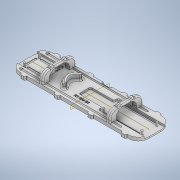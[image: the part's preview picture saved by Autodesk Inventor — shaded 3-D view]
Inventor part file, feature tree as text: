
AUTODESK INVENTOR PART (.ipt)
format: ipt  version: 2021 (Build 250183000, 183)  size: 3,149,312 bytes
history: native  units: in
note: dims shown in document units (in); Inventor stores cm internally (conversion verified against a paired STEP export)
features: fillet x15, extrude x14, sketch x14, mirror x8, plane x2, chamfer x2, revolve x1
ambient origin geometry x8: Origin, YZ Plane, XZ Plane, XY Plane, X Axis, Y Axis, Z Axis, Center Point
bodies: Solid1 (feature_tree)
feature tree (56):
  extrude  "Extrusion1"  Depth=4.9606in
  extrude  "Extrusion2"  TaperAngle=0.0deg  [1 undecoded]
  plane  "Work Plane1"
  plane  "Work Plane2"
  extrude  "Extrusion5"  Depth=0.2362in
  fillet  "Fillet2"  Radius=0.0787in
  mirror  "Mirror3"
  extrude  "Extrusion6"  TaperAngle=0.0deg  [1 undecoded]
  extrude  "Extrusion7"  Depth=0.2362in
  extrude  "Extrusion9"  [1 undecoded]
  extrude  "Extrusion10"  Depth=0.5354in
  fillet  "Fillet4"  Radius=0.9449in
  mirror  "Mirror4"
  mirror  "Mirror5"
  fillet  "Fillet5"  Radius=2.7559in
  extrude  "Extrusion11"  Depth=0.811in
  fillet  "Fillet6"  Radius=0.0866in
  extrude  "Extrusion12"  Depth=0.0945in
  extrude  "Extrusion13"  Depth=0.0945in
  mirror  "Mirror8"
  mirror  "Mirror9"
  mirror  "Mirror10"
  fillet  "Fillet9"  [1 undecoded]
  fillet  "Fillet11"  [1 undecoded]
  fillet  "Fillet12"  [1 undecoded]
  extrude  "Extrusion17"  Depth=0.7in
  fillet  "Fillet16"  Radius=1.8in
  mirror  "Mirror13"
  extrude  "Extrusion20"  Depth=0.1575in TaperAngle=0.0deg
  fillet  "Fillet20"  Radius=1.9685in
  revolve  "Revolution8"  [1 undecoded]
  mirror  "Mirror15"
  extrude  "Extrusion22"  Depth=0.0945in
  extrude  "Extrusion23"  Depth=0.0945in
  chamfer  "Chamfer4"  Distance=0.0945in
  fillet  "Fillet24"  Radius=0.0945in
  fillet  "Fillet25"  [1 undecoded]
  chamfer  "Chamfer5"  [1 undecoded]
  fillet  "Fillet28"  [1 undecoded]
  fillet  "Fillet29"  [1 undecoded]
  fillet  "Fillet30"  Radius=0.9in
  fillet  "Fillet31"  Radius=0.7in
  sketch  "Sketch1"  dims[d0=0.1575in d1=0.0in d2=4.9606in]
  sketch  "Sketch2"  dims[d3=1.5512in d4=0.0in]
  sketch  "Sketch7"  dims[d5=0.0in d6=0.2362in d7=0.0787in d8=0.0in]
  sketch  "Sketch8"  dims[d15=-0.7756in d16=0.0in]
  sketch  "Sketch13"  dims[d17=0.0in d18=0.2362in]
  sketch  "Sketch14"  dims[d19=1.3386in d24=-2.4803in]
  sketch  "Sketch15"  dims[d28=0.5354in d29=0.0in d30=0.5354in d31=0.9449in d32=2.7559in]
  sketch  "Sketch25"  dims[d33=0.4724in d34=0.811in d35=0.0866in d36=0.0in]
  sketch  "Sketch27"  dims[d37=0.0945in d38=0.0945in]
  sketch  "Sketch39"  dims[d39=0.0945in d40=0.0945in d41=0.0in d42=0.0in d43=0.0in]
  sketch  "Sketch44"  dims[d44=0.0in d45=0.7in d46=1.8in]
  sketch  "Sketch47"  dims[d47=0.35in d48=0.1575in d49=0.0in d60=1.9685in]
  sketch  "Sketch49"  dims[d61=0.9449in d62=0.4724in]
  sketch  "Sketch50"  dims[d63=1.7087in d64=0.0945in d65=0.0945in d66=0.0945in d67=0.0945in d68=0.0in d69=0.0in d70=0.0in d71=0.0in d72=0.9in d73=0.7in d74=0.35in d75=0.1969in d79=0.4094in d80=0.0in d81=0.0in d82=0.0in d83=0.0in d84=0.0in d85=0.0787in d86=0.0in d88=0.3543in d89=0.315in d90=0.2362in d92=0.0394in d93=0.0in d96=1.1024in d97=0.5512in d98=0.2756in d99=0.0787in d116=0.2362in d117=0.0in d118=0.0in d119=0.1181in d120=0.0394in d121=0.0in d126=0.0787in d127=0.0157in d128=0.0in d131=0.0394in d133=0.0551in d134=0.0in d138=0.5709in d147=0.2362in d148=0.0591in d171=0.0866in d172=0.0394in d173=0.0394in d174=0.0866in d175=0.2638in d176=0.0866in d177=0.0945in d178=0.0866in d179=0.0394in d180=0.0394in d181=0.0787in d182=0.0236in d183=0.0in d184=0.0433in d204=0.0945in d211=0.3937in d212=0.0in d213=0.0787in d214=4.4094in d215=0.0in d216=0.0394in d228=180.0deg d229=0.0394in d230=0.0197in d232=0.0in d233=0.0394in d240=0.0in d243=0.0in d244=0.0in d245=0.0in d246=0.1575in d247=0.1575in d248=0.315in d249=0.315in d250=0.0in d253=0.3937in d254=0.0787in d255=0.1969in d256=0.0787in d257=0.0in d258=0.0787in d259=0.0394in d260=45.0deg d261=0.0787in d262=0.0394in d263=0.8661in d264=0.4331in d265=0.6575in d266=0.3287in d267=0.1181in d268=0.1575in d269=45.0deg d272=0.1213in d273=0.0394in d274=0.2819in d275=0.0591in d276=0.0394in d277=0.0787in d146=0.0197in d149=0.0344in]
note: 11 required parameter values undecoded (feature->parameter linkage not recoverable at this tier; creation-order binding heuristic only, values carry confidence <= 0.55)